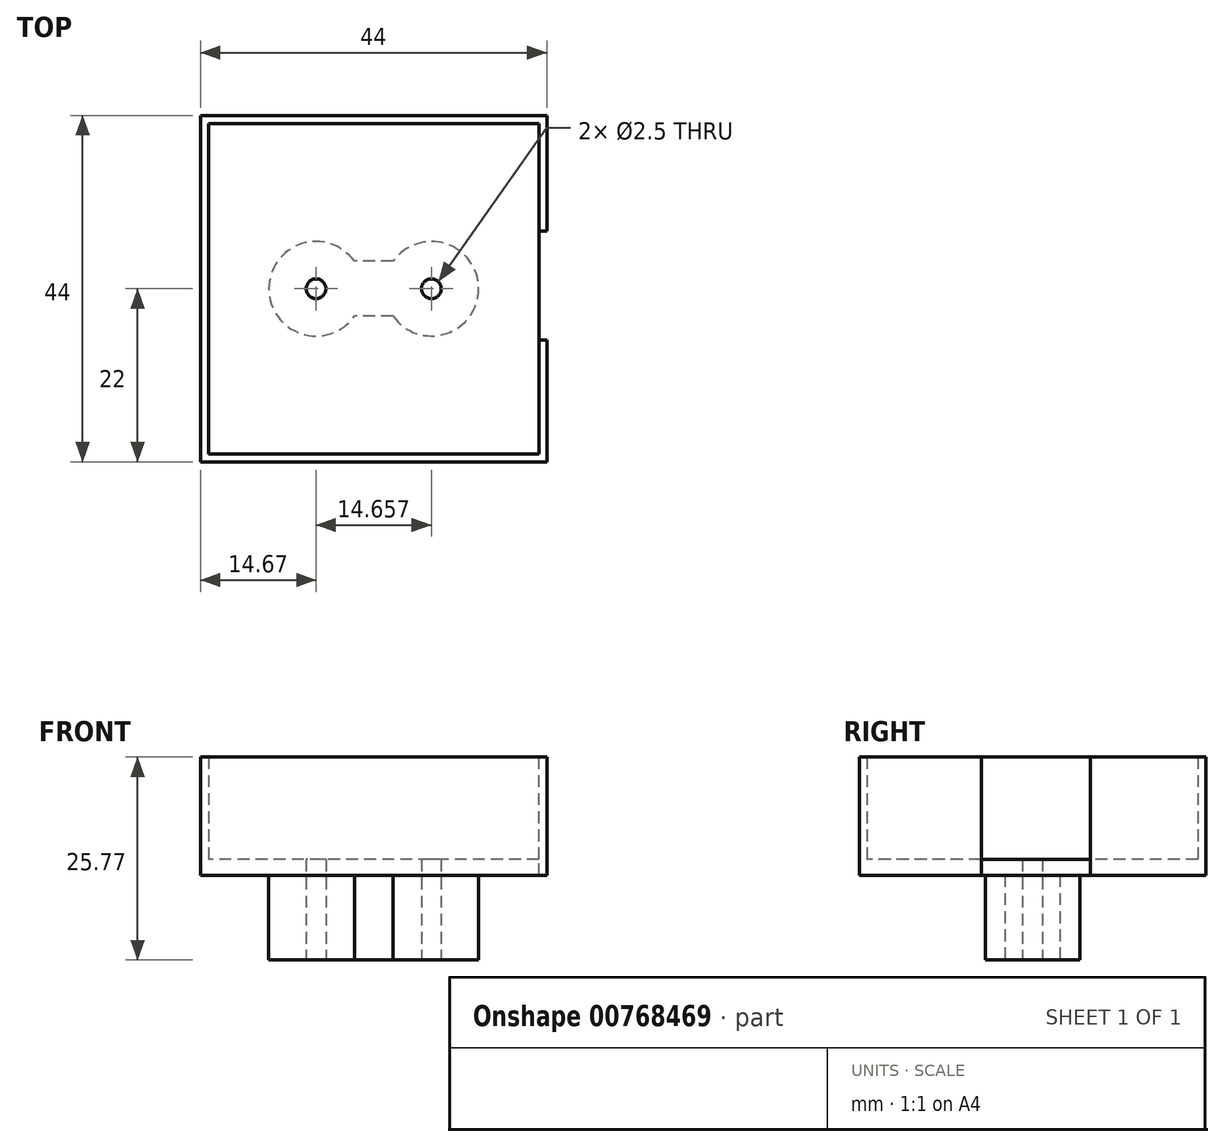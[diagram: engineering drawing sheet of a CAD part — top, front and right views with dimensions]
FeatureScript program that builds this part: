
annotation { "Feature Type Name" : "Feature", "Feature Type Description" : "" }
export const myFeature = defineFeature(function(context is Context, id is Id, definition is map)
    precondition{}
    {
        {
            var Q0;
            Q0=qCreatedBy(makeId("Top.planeOp"),FACE);
            var sketch = newSketch(context, id + "F0", { "sketchPlane" : qUnion([Q0])});
            skCircle(sketch, "E0", {"center": v(0, 0) * mm, "radius": 6 * mm});
            skCircle(sketch, "E1", {"center": v(14.66, 0) * mm, "radius": 6 * mm});
            skLineSegment(sketch, "E2.bottom", {"start": v(14.66, 3.5) * mm, "end": v(0.07, 3.5) * mm});
            skLineSegment(sketch, "E2.top", {"start": v(14.66, -3.5) * mm, "end": v(0.07, -3.5) * mm});
            skLineSegment(sketch, "E2.left", {"start": v(14.66, 3.5) * mm, "end": v(14.66, -3.5) * mm});
            skLineSegment(sketch, "E2.right", {"start": v(0.07, 3.5) * mm, "end": v(0.07, -3.5) * mm});
            skPoint(sketch, "E2.middle", {"position": v(7.37, 0) * mm});
            skSolve(sketch);
        }
        {
            var Q0;
            {var subQ5=sQuery(id+"F0.wireOp",EDGE,"E2.right");Q0=makeQuery(id+"F0.imprint","IMPRINT",FACE,{"disambiguationData":[TD([[makeQuery(id+"F0.imprint","IMPRINT",EDGE,{"derivedFrom":subQ5}),-1.0]])]});}
            var Q1;
            {var subQ0=sQuery(id+"F0.wireOp",EDGE,"E2.bottom");var subQ1=sQuery(id+"F0.wireOp",EDGE,"E0");var subQ2=makeQuery(id+"F0.imprint","INTERSECT",VERTEX,{"derivedFrom":[subQ1,subQ0]});Q1=makeQuery(id+"F0.imprint","IMPRINT",FACE,{"disambiguationData":[TD([[makeQuery(id+"F0.imprint","IMPRINT",EDGE,{"disambiguationData":[TD([[subQ2,1.0]])],"derivedFrom":subQ1}),-1.0]])]});}
            var Q2;
            {var subQ5=sQuery(id+"F0.wireOp",EDGE,"E2.right");Q2=makeQuery(id+"F0.imprint","IMPRINT",FACE,{"disambiguationData":[TD([[makeQuery(id+"F0.imprint","IMPRINT",EDGE,{"derivedFrom":subQ5}),1.0]])]});}
            var Q3;
            {var subQ5=sQuery(id+"F0.wireOp",EDGE,"E2.left");Q3=makeQuery(id+"F0.imprint","IMPRINT",FACE,{"disambiguationData":[TD([[makeQuery(id+"F0.imprint","IMPRINT",EDGE,{"derivedFrom":subQ5}),-1.0]])]});}
            var Q4;
            {var subQ5=sQuery(id+"F0.wireOp",EDGE,"E2.left");Q4=makeQuery(id+"F0.imprint","IMPRINT",FACE,{"disambiguationData":[TD([[makeQuery(id+"F0.imprint","IMPRINT",EDGE,{"derivedFrom":subQ5}),1.0]])]});}
            extrude(context, id + "F1", {"entities" : qUnion([Q0, Q1, Q2, Q3, Q4]), "depth" : 16.65 * mm, "offsetDistance" : 25 * mm});
        }
        {
            var Q0;
            Q0=makeQuery(id+"F1.opExtrude","CAP_FACE",FACE,{"disambiguationData":[OSD([sQuery(id+"F0.wireOp",EDGE,"E0"),sQuery(id+"F0.wireOp",EDGE,"E1"),sQuery(id+"F0.wireOp",EDGE,"E2.bottom"),sQuery(id+"F0.wireOp",EDGE,"E2.top")])],"isStart":false});
            var sketch = newSketch(context, id + "F2", { "sketchPlane" : qUnion([Q0])});
            skLineSegment(sketch, "E3", {"start": v(0, 0) * mm, "end": v(14.66, 0) * mm});
            skPoint(sketch, "E4", {"position": v(7.33, 0) * mm});
            skLineSegment(sketch, "E5.bottom", {"start": v(29.33, 22) * mm, "end": v(-14.67, 22) * mm});
            skLineSegment(sketch, "E5.top", {"start": v(29.33, -22) * mm, "end": v(-14.67, -22) * mm});
            skLineSegment(sketch, "E5.left", {"start": v(29.33, 22) * mm, "end": v(29.33, -22) * mm});
            skLineSegment(sketch, "E5.right", {"start": v(-14.67, 22) * mm, "end": v(-14.67, -22) * mm});
            skLineSegment(sketch, "E6.bottom", {"start": v(28.33, 21) * mm, "end": v(-13.67, 21) * mm});
            skLineSegment(sketch, "E6.top", {"start": v(28.33, -21) * mm, "end": v(-13.67, -21) * mm});
            skLineSegment(sketch, "E6.left", {"start": v(28.33, 21) * mm, "end": v(28.33, -21) * mm});
            skLineSegment(sketch, "E6.right", {"start": v(-13.67, 21) * mm, "end": v(-13.67, -21) * mm});
            skSolve(sketch);
        }
        {
            var Q0;
            Q0=makeQuery(id+"F2.imprint","IMPRINT",FACE,{"disambiguationData":[TD([[makeQuery(id+"F2.imprint","IMPRINT",EDGE,{"derivedFrom":sQuery(id+"F2.wireOp",EDGE,"E6.bottom")}),1.0]])]});
            var Q1;
            Q1=makeQuery(id+"F2.imprint","IMPRINT",FACE,{"disambiguationData":[TD([[makeQuery(id+"F2.imprint","IMPRINT",EDGE,{"derivedFrom":makeQuery(id+"F1.opExtrude","CAP_EDGE",EDGE,{"disambiguationData":[OSD([sQuery(id+"F0.wireOp",EDGE,"E0")])],"isStart":false})}),1.0]])]});
            extrude(context, id + "F3", {"entities" : qUnion([Q0, Q1]), "operationType" : NewBodyOperationType.ADD, "depth" : 2 * mm, "offsetDistance" : 25 * mm});
        }
        {
            var Q0;
            Q0 = qSketchRegion(id + "F2", true);
            extrude(context, id + "F4", {"entities" : qUnion([Q0]), "operationType" : NewBodyOperationType.ADD, "depth" : 15 * mm, "offsetDistance" : 25 * mm});
        }
        {
            var Q0;
            Q0=makeQuery(id+"F1.opExtrude","CAP_FACE",FACE,{"disambiguationData":[OSD([sQuery(id+"F0.wireOp",EDGE,"E0"),sQuery(id+"F0.wireOp",EDGE,"E1"),sQuery(id+"F0.wireOp",EDGE,"E2.bottom"),sQuery(id+"F0.wireOp",EDGE,"E2.top")])],"isStart":true});
            var sketch = newSketch(context, id + "F5", { "sketchPlane" : qUnion([Q0])});
            skPoint(sketch, "E7", {"position": v(0, 0) * mm});
            skPoint(sketch, "E8", {"position": v(14.66, 0) * mm});
            skSolve(sketch);
        }
        {
            var Q0;
            Q0=sQuery(id+"F5.wireOp",VERTEX,"E7");
            var Q1;
            Q1=sQuery(id+"F5.wireOp",VERTEX,"E8");
            var Q2;
            Q2=makeQuery(id+"F1.opExtrude","SWEPT_BODY",BODY,{"disambiguationData":[OSD([sQuery(id+"F0.wireOp",EDGE,"E0"),sQuery(id+"F0.wireOp",EDGE,"E1"),sQuery(id+"F0.wireOp",EDGE,"E2.bottom"),sQuery(id+"F0.wireOp",EDGE,"E2.top")])]});
            hole(context, id + "F6", {"style" : HoleStyle.SIMPLE, "endStyle" : HoleEndStyle.THROUGH, "standardTappedOrClearance" : lookupTablePath({ "standard" : "ISO", "engagement" : "75%", "pitch" : "0.5 mm", "size" : "M3", "type" : "Tapped" }), "standardBlindInLast" : lookupTablePath({ "standard" : "ISO", "fit" : "Normal", "engagement" : "75%", "pitch" : "0.5 mm", "size" : "M3", "type" : "Clearance & tapped" }), "holeDiameter" : 2.5 * mm, "majorDiameter" : 3 * mm, "showTappedDepth" : true, "isTappedThrough" : true, "tappedDepth" : 12 * mm, "tapClearance" : 3, "locations" : qUnion([Q0, Q1]), "scope" : qUnion([Q2])});
        }
        {
            var Q0;
            Q0=makeQuery(id+"F1.opExtrude","CAP_FACE",FACE,{"disambiguationData":[OSD([sQuery(id+"F0.wireOp",EDGE,"E0"),sQuery(id+"F0.wireOp",EDGE,"E1"),sQuery(id+"F0.wireOp",EDGE,"E2.bottom"),sQuery(id+"F0.wireOp",EDGE,"E2.top")])],"isStart":true});
            extrude(context, id + "F7", {"entities" : qUnion([Q0]), "operationType" : NewBodyOperationType.REMOVE, "oppositeDirection" : true, "depth" : 5.88 * mm, "offsetDistance" : 25 * mm});
        }
        {
            var Q0;
            Q0=makeQuery(id+"F4.opExtrude","CAP_FACE",FACE,{"disambiguationData":[OSD([sQuery(id+"F2.wireOp",EDGE,"E5.bottom"),sQuery(id+"F2.wireOp",EDGE,"E5.top"),sQuery(id+"F2.wireOp",EDGE,"E5.left"),sQuery(id+"F2.wireOp",EDGE,"E5.right"),sQuery(id+"F2.wireOp",EDGE,"E6.bottom"),sQuery(id+"F2.wireOp",EDGE,"E6.top"),sQuery(id+"F2.wireOp",EDGE,"E6.left"),sQuery(id+"F2.wireOp",EDGE,"E6.right")])],"isStart":false});
            var sketch = newSketch(context, id + "F8", { "sketchPlane" : qUnion([Q0])});
            skLineSegment(sketch, "E9", {"start": v(28.33, -6.5) * mm, "end": v(29.33, -6.5) * mm});
            skLineSegment(sketch, "E10", {"start": v(28.33, 7.32) * mm, "end": v(29.33, 7.32) * mm});
            skSolve(sketch);
        }
        {
            var Q0;
            Q0 = qSketchRegion(id + "F8", true);
            var Q1;
            {var subQ0=sQuery(id+"F8.wireOp",EDGE,"E9");Q1=makeQuery(id+"F8.imprint","IMPRINT",FACE,{"disambiguationData":[TD([[makeQuery(id+"F8.imprint","IMPRINT",EDGE,{"derivedFrom":subQ0}),1.0]])]});}
            extrude(context, id + "F9", {"entities" : qUnion([Q0, Q1]), "operationType" : NewBodyOperationType.REMOVE, "oppositeDirection" : true, "depth" : 25 * mm, "offsetDistance" : 25 * mm});
        }
    });
